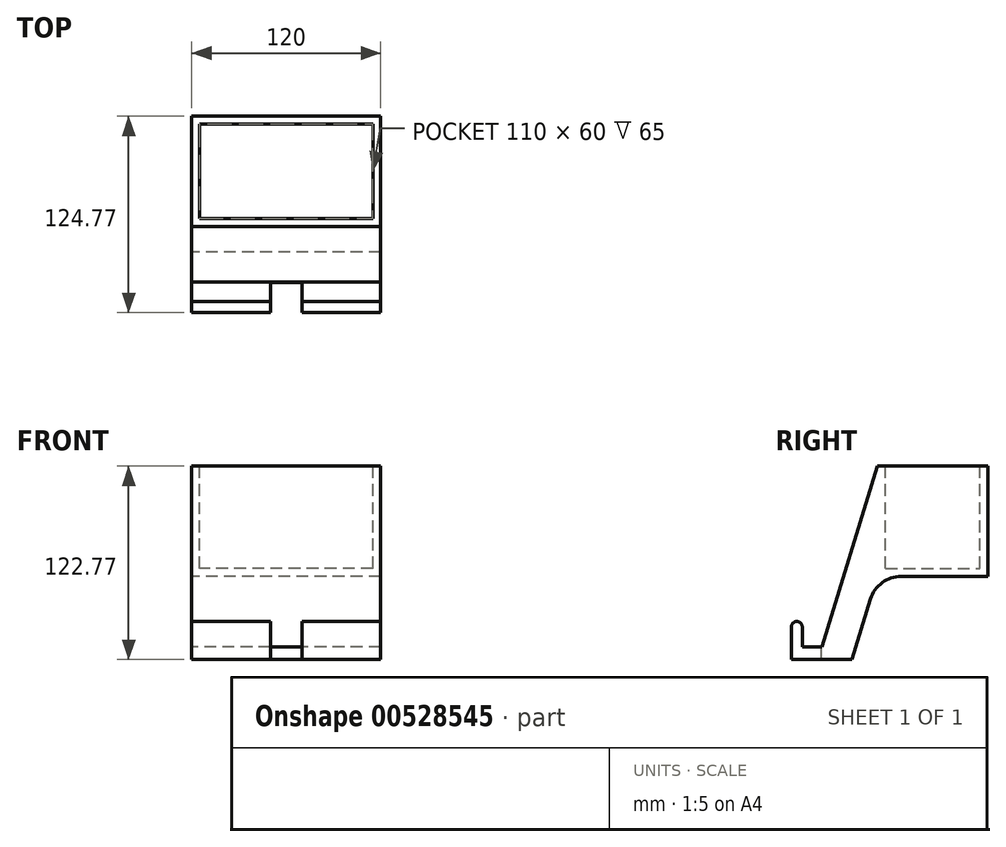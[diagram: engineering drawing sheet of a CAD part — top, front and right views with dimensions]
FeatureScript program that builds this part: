
annotation { "Feature Type Name" : "Feature", "Feature Type Description" : "" }
export const myFeature = defineFeature(function(context is Context, id is Id, definition is map)
    precondition{}
    {
        {
            var Q0;
            Q0=qCreatedBy(makeId("Right.planeOp"),FACE);
            var sketch = newSketch(context, id + "F0", { "sketchPlane" : qUnion([Q0])});
            skLineSegment(sketch, "E0.bottom", {"start": v(-34.9, 32.42) * mm, "end": v(35.1, 32.42) * mm});
            skLineSegment(sketch, "E0.top", {"start": v(-34.9, -37.58) * mm, "end": v(35.1, -37.58) * mm});
            skLineSegment(sketch, "E0.left", {"start": v(-34.9, 32.42) * mm, "end": v(-34.9, -37.58) * mm});
            skLineSegment(sketch, "E0.right", {"start": v(35.1, 32.42) * mm, "end": v(35.1, -37.58) * mm});
            skLineSegment(sketch, "E1", {"start": v(-34.9, 32.42) * mm, "end": v(-70.19, -82.35) * mm});
            skLineSegment(sketch, "E2", {"start": v(-70.19, -82.35) * mm, "end": v(-82.67, -82.35) * mm});
            skLineSegment(sketch, "E3", {"start": v(-82.67, -82.35) * mm, "end": v(-82.67, -66.3) * mm});
            skLineSegment(sketch, "E4", {"start": v(-82.67, -66.3) * mm, "end": v(-89.67, -66.3) * mm});
            skLineSegment(sketch, "E5", {"start": v(-89.67, -66.3) * mm, "end": v(-89.67, -82.35) * mm});
            skLineSegment(sketch, "E6", {"start": v(-89.67, -82.35) * mm, "end": v(-89.67, -90.35) * mm});
            skLineSegment(sketch, "E7", {"start": v(-89.67, -90.35) * mm, "end": v(-70.19, -90.35) * mm});
            skLineSegment(sketch, "E8", {"start": v(-34.9, -37.58) * mm, "end": v(-51.13, -90.35) * mm});
            skLineSegment(sketch, "E9", {"start": v(-51.13, -90.35) * mm, "end": v(-70.19, -90.35) * mm});
            skSolve(sketch);
        }
        {
            var Q0;
            Q0 = qSketchRegion(id + "F0", true);
            extrude(context, id + "F1", {"entities" : qUnion([Q0]), "depth" : 120 * mm, "offsetDistance" : 25 * mm});
        }
        {
            var Q0;
            Q0=makeQuery(id+"F1.opExtrude","SWEPT_FACE",FACE,{"disambiguationData":[OSD([sQuery(id+"F0.wireOp",EDGE,"E0.bottom")])]});
            var sketch = newSketch(context, id + "F2", { "sketchPlane" : qUnion([Q0])});
            skLineSegment(sketch, "E10", {"start": v(115, 30.1) * mm, "end": v(5, 30.1) * mm});
            skLineSegment(sketch, "E11", {"start": v(5, 30.1) * mm, "end": v(5, -29.9) * mm});
            skLineSegment(sketch, "E12", {"start": v(5, -29.9) * mm, "end": v(115, -29.9) * mm});
            skLineSegment(sketch, "E13", {"start": v(115, -29.9) * mm, "end": v(115, 30.1) * mm});
            skSolve(sketch);
        }
        {
            var Q0;
            Q0 = qSketchRegion(id + "F2", true);
            extrude(context, id + "F3", {"entities" : qUnion([Q0]), "operationType" : NewBodyOperationType.REMOVE, "oppositeDirection" : true, "depth" : 65 * mm, "offsetDistance" : 25 * mm});
        }
        {
            var Q0;
            Q0=makeQuery(id+"F1.opExtrude","SWEPT_FACE",FACE,{"disambiguationData":[OSD([sQuery(id+"F0.wireOp",EDGE,"E5"),sQuery(id+"F0.wireOp",EDGE,"E6")])]});
            var sketch = newSketch(context, id + "F4", { "sketchPlane" : qUnion([Q0])});
            skLineSegment(sketch, "E14", {"start": v(50, -90.35) * mm, "end": v(50, -66.3) * mm});
            skLineSegment(sketch, "E15", {"start": v(50, -66.3) * mm, "end": v(70, -66.3) * mm});
            skLineSegment(sketch, "E16", {"start": v(70, -66.3) * mm, "end": v(70, -90.35) * mm});
            skLineSegment(sketch, "E17", {"start": v(50, -90.35) * mm, "end": v(70, -90.35) * mm});
            skSolve(sketch);
        }
        {
            var Q0;
            Q0=makeQuery(id+"F4.imprint","IMPRINT",FACE,{"disambiguationData":[TD([[makeQuery(id+"F4.imprint","IMPRINT",EDGE,{"derivedFrom":sQuery(id+"F4.wireOp",EDGE,"E14")}),-1.0]])]});
            extrude(context, id + "F5", {"entities" : qUnion([Q0]), "operationType" : NewBodyOperationType.REMOVE, "oppositeDirection" : true, "depth" : 19 * mm, "offsetDistance" : 25 * mm});
        }
        {
            var Q0;
            Q0=makeQuery(id+"F1.opExtrude","SWEPT_EDGE",EDGE,{"disambiguationData":[OSD([sQuery(id+"F0.wireOp",EDGE,"E0.top"),sQuery(id+"F0.wireOp",EDGE,"E0.left"),sQuery(id+"F0.wireOp",EDGE,"E8")])]});
            fillet(context, id + "F6", {"entities" : qUnion([Q0]), "radius" : 20.55 * mm, "tangentPropagation" : true, "allowEdgeOverflow" : false});
        }
        {
            var Q0;
            {var subQ0=sQuery(id+"F0.wireOp",EDGE,"E4");var subQ1=sQuery(id+"F0.wireOp",EDGE,"E3");Q0=makeQuery(id+"F5.boolean.opBoolean","SPLIT",EDGE,{"disambiguationData":[TD([makeQuery(id+"F5.opExtrude","SWEPT_FACE",FACE,{"disambiguationData":[OSD([sQuery(id+"F4.wireOp",EDGE,"E16")])]})])],"derivedFrom":makeQuery(id+"F1.opExtrude","SWEPT_EDGE",EDGE,{"disambiguationData":[OSD([subQ1,subQ0])]})});}
            var Q1;
            {var subQ0=sQuery(id+"F0.wireOp",EDGE,"E4");var subQ1=sQuery(id+"F0.wireOp",EDGE,"E3");Q1=makeQuery(id+"F5.boolean.opBoolean","SPLIT",EDGE,{"disambiguationData":[TD([makeQuery(id+"F5.opExtrude","SWEPT_FACE",FACE,{"disambiguationData":[OSD([sQuery(id+"F4.wireOp",EDGE,"E14")])]})])],"derivedFrom":makeQuery(id+"F1.opExtrude","SWEPT_EDGE",EDGE,{"disambiguationData":[OSD([subQ1,subQ0])]})});}
            var Q2;
            {var subQ1=sQuery(id+"F0.wireOp",EDGE,"E5");var subQ2=sQuery(id+"F0.wireOp",EDGE,"E4");Q2=makeQuery(id+"F5.boolean.opBoolean","SPLIT",EDGE,{"disambiguationData":[TD([makeQuery(id+"F5.opExtrude","SWEPT_FACE",FACE,{"disambiguationData":[OSD([sQuery(id+"F4.wireOp",EDGE,"E14")])]})])],"derivedFrom":makeQuery(id+"F1.opExtrude","SWEPT_EDGE",EDGE,{"disambiguationData":[OSD([subQ2,subQ1])]})});}
            var Q3;
            {var subQ1=sQuery(id+"F0.wireOp",EDGE,"E5");var subQ2=sQuery(id+"F0.wireOp",EDGE,"E4");Q3=makeQuery(id+"F5.boolean.opBoolean","SPLIT",EDGE,{"disambiguationData":[TD([makeQuery(id+"F5.opExtrude","SWEPT_FACE",FACE,{"disambiguationData":[OSD([sQuery(id+"F4.wireOp",EDGE,"E16")])]})])],"derivedFrom":makeQuery(id+"F1.opExtrude","SWEPT_EDGE",EDGE,{"disambiguationData":[OSD([subQ2,subQ1])]})});}
            fillet(context, id + "F7", {"entities" : qUnion([Q0, Q1, Q2, Q3]), "radius" : 3.5 * mm, "tangentPropagation" : true, "allowEdgeOverflow" : false});
        }
    });
